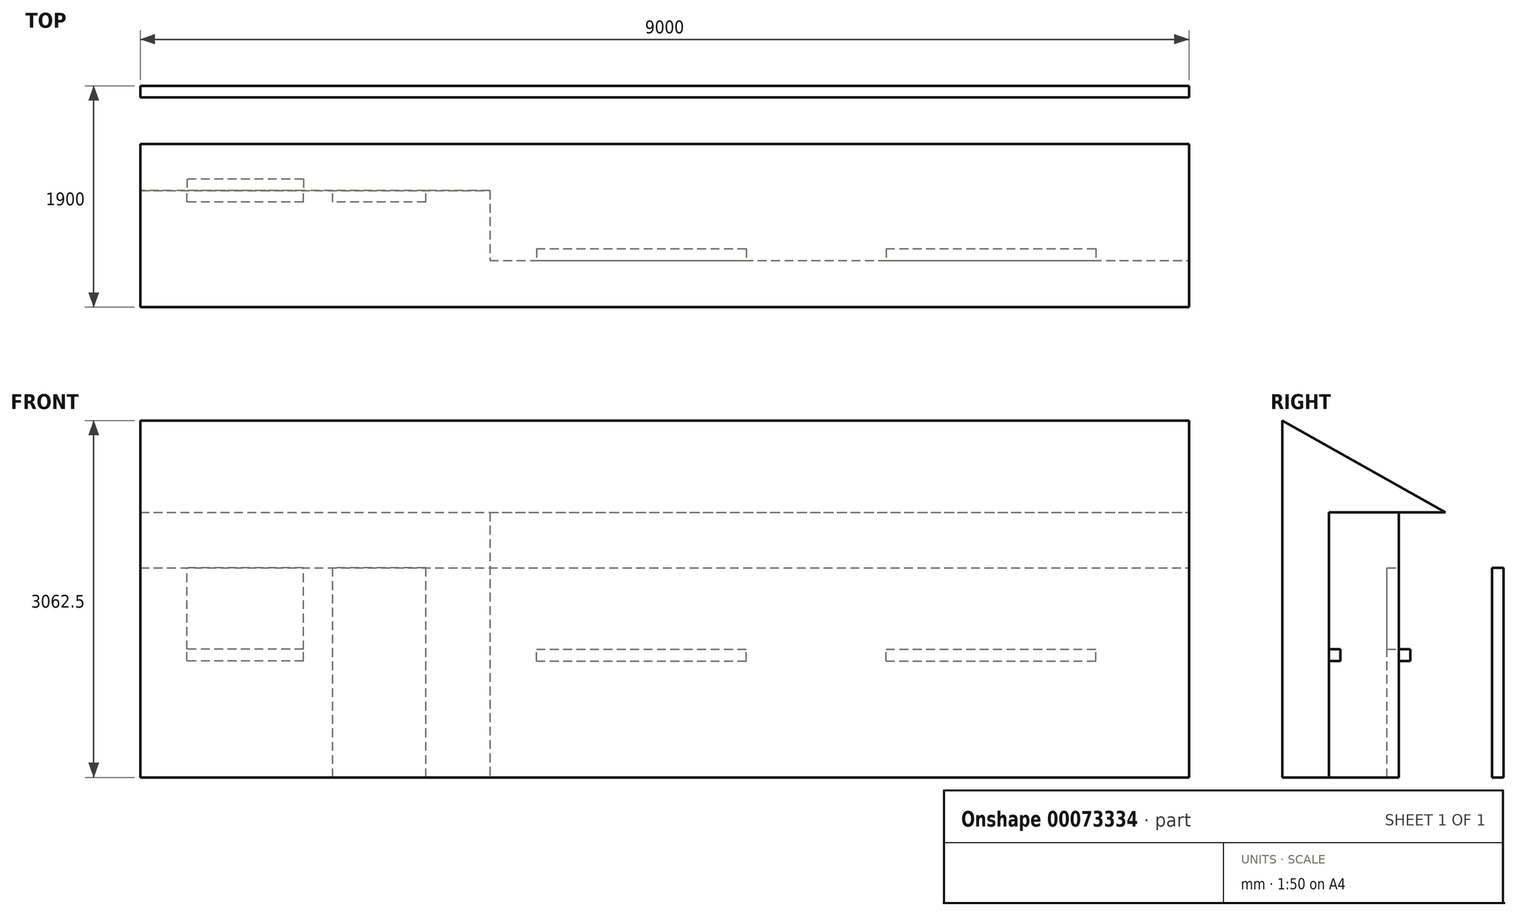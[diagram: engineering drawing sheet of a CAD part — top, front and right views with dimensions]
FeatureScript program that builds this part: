
annotation { "Feature Type Name" : "Feature", "Feature Type Description" : "" }
export const myFeature = defineFeature(function(context is Context, id is Id, definition is map)
    precondition{}
    {
        {
            var Q0;
            Q0=qCreatedBy(makeId("Top.planeOp"),FACE);
            var sketch = newSketch(context, id + "F0", { "sketchPlane" : qUnion([Q0])});
            skLineSegment(sketch, "E0", {"start": v(0, 0) * mm, "end": v(9000, 0) * mm});
            skLineSegment(sketch, "E1", {"start": v(9000, 0) * mm, "end": v(9000, 400) * mm});
            skLineSegment(sketch, "E2", {"start": v(9000, 400) * mm, "end": v(3000, 400) * mm});
            skLineSegment(sketch, "E3", {"start": v(3000, 400) * mm, "end": v(3000, 1000) * mm});
            skLineSegment(sketch, "E4", {"start": v(3000, 1000) * mm, "end": v(0, 1000) * mm});
            skLineSegment(sketch, "E5", {"start": v(0, 1000) * mm, "end": v(0, 0) * mm});
            skLineSegment(sketch, "E6.bottom", {"start": v(0, 1800) * mm, "end": v(9000, 1800) * mm});
            skLineSegment(sketch, "E6.top", {"start": v(0, 1900) * mm, "end": v(9000, 1900) * mm});
            skLineSegment(sketch, "E6.left", {"start": v(0, 1800) * mm, "end": v(0, 1900) * mm});
            skLineSegment(sketch, "E6.right", {"start": v(9000, 1800) * mm, "end": v(9000, 1900) * mm});
            skSolve(sketch);
        }
        {
            var Q0;
            Q0=makeQuery(id+"F0.imprint","IMPRINT",FACE,{"disambiguationData":[TD([[makeQuery(id+"F0.imprint","IMPRINT",EDGE,{"derivedFrom":sQuery(id+"F0.wireOp",EDGE,"E0")}),1.0]])]});
            extrude(context, id + "F1", {"entities" : qUnion([Q0]), "depth" : 2500 * mm});
        }
        {
            var Q0;
            Q0=makeQuery(id+"F0.imprint","IMPRINT",FACE,{"disambiguationData":[TD([[makeQuery(id+"F0.imprint","IMPRINT",EDGE,{"derivedFrom":sQuery(id+"F0.wireOp",EDGE,"E6.bottom")}),1.0]])]});
            extrude(context, id + "F2", {"entities" : qUnion([Q0]), "depth" : 1800 * mm});
        }
        {
            var Q0;
            Q0=makeQuery(id+"F1.opExtrude","SWEPT_FACE",FACE,{"disambiguationData":[OSD([sQuery(id+"F0.wireOp",EDGE,"E4")])]});
            var sketch = newSketch(context, id + "F3", { "sketchPlane" : qUnion([Q0])});
            skLineSegment(sketch, "E7.bottom", {"start": v(-1400, 1000) * mm, "end": v(-400, 1000) * mm});
            skLineSegment(sketch, "E7.top", {"start": v(-1400, 1100) * mm, "end": v(-400, 1100) * mm});
            skLineSegment(sketch, "E7.left", {"start": v(-1400, 1000) * mm, "end": v(-1400, 1100) * mm});
            skLineSegment(sketch, "E7.right", {"start": v(-400, 1000) * mm, "end": v(-400, 1100) * mm});
            skSolve(sketch);
        }
        {
            var Q0;
            Q0=makeQuery(id+"F3.imprint","IMPRINT",FACE,{"disambiguationData":[TD([[makeQuery(id+"F3.imprint","IMPRINT",EDGE,{"derivedFrom":sQuery(id+"F3.wireOp",EDGE,"E7.bottom")}),1.0]])]});
            extrude(context, id + "F4", {"entities" : qUnion([Q0]), "operationType" : NewBodyOperationType.ADD, "depth" : 100 * mm});
        }
        {
            var Q0;
            Q0=makeQuery(id+"F1.opExtrude","SWEPT_FACE",FACE,{"disambiguationData":[OSD([sQuery(id+"F0.wireOp",EDGE,"E4")])]});
            var sketch = newSketch(context, id + "F5", { "sketchPlane" : qUnion([Q0])});
            skLineSegment(sketch, "E8.bottom", {"start": v(-1400, 1100) * mm, "end": v(-400, 1100) * mm});
            skLineSegment(sketch, "E8.top", {"start": v(-1400, 1800) * mm, "end": v(-400, 1800) * mm});
            skLineSegment(sketch, "E8.left", {"start": v(-1400, 1100) * mm, "end": v(-1400, 1800) * mm});
            skLineSegment(sketch, "E8.right", {"start": v(-400, 1100) * mm, "end": v(-400, 1800) * mm});
            skLineSegment(sketch, "E9.bottom", {"start": v(-2450, 0) * mm, "end": v(-1650, 0) * mm});
            skLineSegment(sketch, "E9.top", {"start": v(-2450, 1800) * mm, "end": v(-1650, 1800) * mm});
            skLineSegment(sketch, "E9.left", {"start": v(-2450, 0) * mm, "end": v(-2450, 1800) * mm});
            skLineSegment(sketch, "E9.right", {"start": v(-1650, 0) * mm, "end": v(-1650, 1800) * mm});
            skSolve(sketch);
        }
        {
            var Q0;
            Q0 = qSketchRegion(id + "F5", true);
            extrude(context, id + "F6", {"entities" : qUnion([Q0]), "operationType" : NewBodyOperationType.REMOVE, "oppositeDirection" : true, "depth" : 100 * mm});
        }
        {
            var Q0;
            Q0=makeQuery(id+"F1.opExtrude","SWEPT_FACE",FACE,{"disambiguationData":[OSD([sQuery(id+"F0.wireOp",EDGE,"E2")])]});
            var sketch = newSketch(context, id + "F7", { "sketchPlane" : qUnion([Q0])});
            skLineSegment(sketch, "E10.bottom", {"start": v(-3400, 1000) * mm, "end": v(-5200, 1000) * mm});
            skLineSegment(sketch, "E10.top", {"start": v(-3400, 1100) * mm, "end": v(-5200, 1100) * mm});
            skLineSegment(sketch, "E10.left", {"start": v(-3400, 1000) * mm, "end": v(-3400, 1100) * mm});
            skLineSegment(sketch, "E10.right", {"start": v(-5200, 1000) * mm, "end": v(-5200, 1100) * mm});
            skLineSegment(sketch, "E11.bottom", {"start": v(-6400, 1000) * mm, "end": v(-8200, 1000) * mm});
            skLineSegment(sketch, "E11.top", {"start": v(-6400, 1100) * mm, "end": v(-8200, 1100) * mm});
            skLineSegment(sketch, "E11.left", {"start": v(-6400, 1000) * mm, "end": v(-6400, 1100) * mm});
            skLineSegment(sketch, "E11.right", {"start": v(-8200, 1000) * mm, "end": v(-8200, 1100) * mm});
            skSolve(sketch);
        }
        {
            var Q0;
            Q0 = qSketchRegion(id + "F7", true);
            extrude(context, id + "F8", {"entities" : qUnion([Q0]), "operationType" : NewBodyOperationType.ADD, "depth" : 100 * mm});
        }
        {
            var Q0;
            Q0=makeQuery(id+"F1.opExtrude","SWEPT_FACE",FACE,{"disambiguationData":[OSD([sQuery(id+"F0.wireOp",EDGE,"E1")])]});
            var sketch = newSketch(context, id + "F9", { "sketchPlane" : qUnion([Q0])});
            skLineSegment(sketch, "E12", {"start": v(400, 2275) * mm, "end": v(1400, 2275) * mm});
            skLineSegment(sketch, "E13", {"start": v(1400, 2275) * mm, "end": v(0, 3062.5) * mm});
            skLineSegment(sketch, "E14", {"start": v(0, 3062.5) * mm, "end": v(0, 2275) * mm});
            skLineSegment(sketch, "E15", {"start": v(0, 2275) * mm, "end": v(400, 2275) * mm});
            skSolve(sketch);
        }
        {
            var Q0;
            {var subQ4=sQuery(id+"F9.wireOp",EDGE,"E12");Q0=makeQuery(id+"F9.imprint","IMPRINT",FACE,{"disambiguationData":[TD([[makeQuery(id+"F9.imprint","IMPRINT",EDGE,{"derivedFrom":subQ4}),1.0]])]});}
            var Q1;
            Q1=makeQuery(id+"F1.opExtrude","SWEPT_FACE",FACE,{"disambiguationData":[OSD([sQuery(id+"F0.wireOp",EDGE,"E5")])]});
            extrude(context, id + "F10", {"entities" : qUnion([Q0]), "operationType" : NewBodyOperationType.ADD, "endBound" : BoundingType.UP_TO_SURFACE, "oppositeDirection" : true, "endBoundEntityFace" : qUnion([Q1]), "depth" : 25 * mm});
        }
    });
